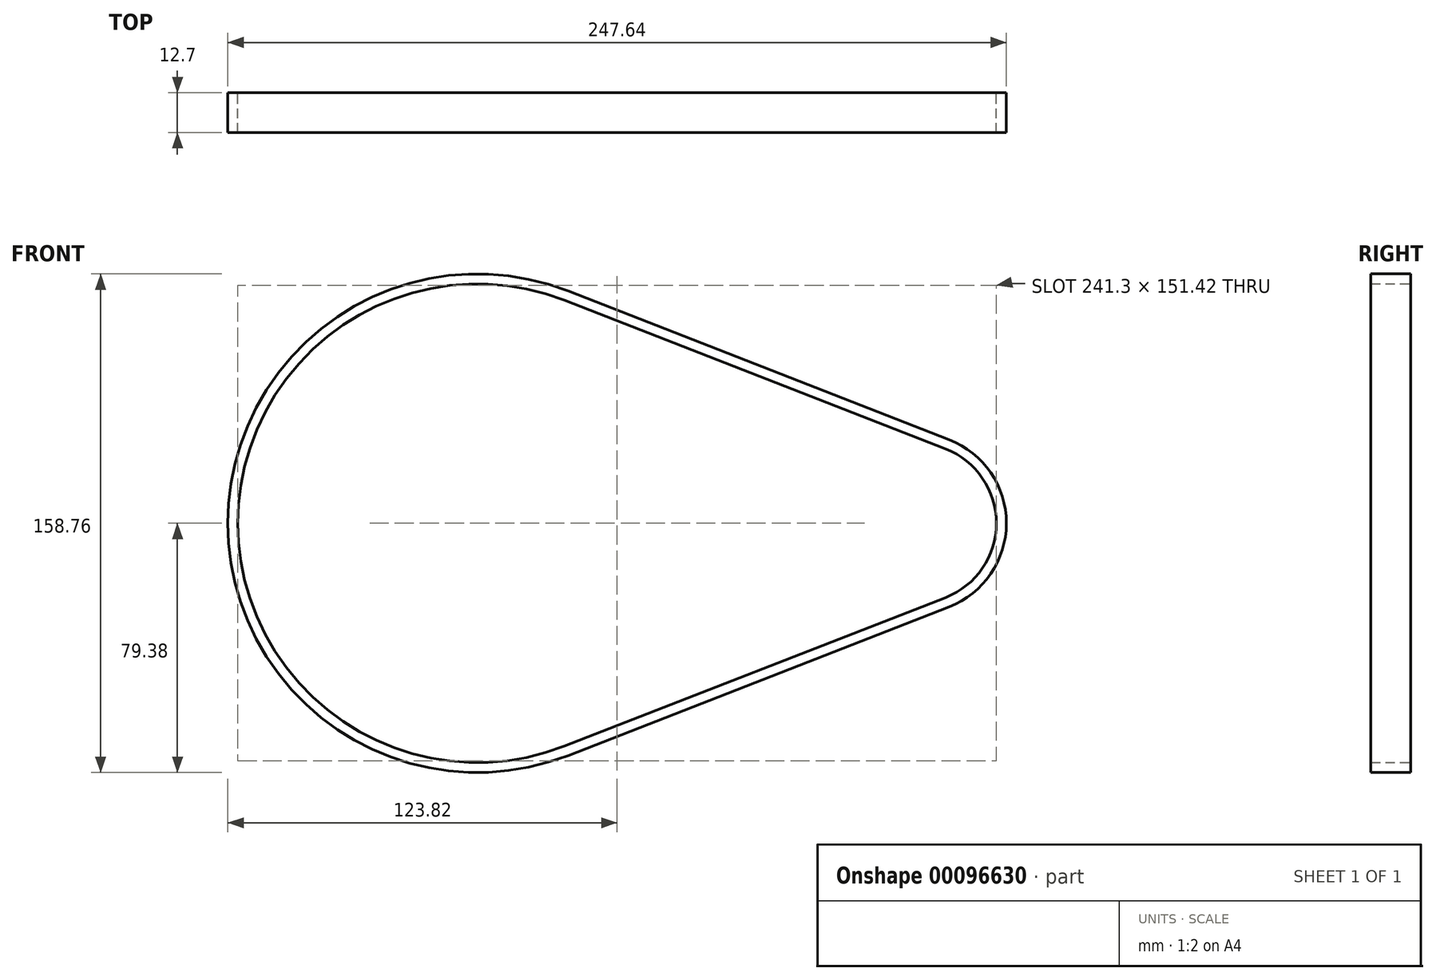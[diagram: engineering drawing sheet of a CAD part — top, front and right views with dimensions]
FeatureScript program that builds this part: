
annotation { "Feature Type Name" : "Feature", "Feature Type Description" : "" }
export const myFeature = defineFeature(function(context is Context, id is Id, definition is map)
    precondition{}
    {
        {
            var Q0;
            Q0=qCreatedBy(makeId("Front.planeOp"),FACE);
            var sketch = newSketch(context, id + "F0", { "sketchPlane" : qUnion([Q0])});
            skArc(sketch, "E0", {"start": v(27.7, 70.98) * mm, "mid": v(-76.2, 0) * mm, "end": v(27.7, -70.98) * mm});
            skArc(sketch, "E1", {"start": v(148.94, -23.66) * mm, "mid": v(165.1, 0) * mm, "end": v(148.94, 23.66) * mm});
            skLineSegment(sketch, "E2", {"start": v(27.7, 70.98) * mm, "end": v(148.94, 23.66) * mm});
            skLineSegment(sketch, "E3", {"start": v(27.7, -70.98) * mm, "end": v(148.94, -23.66) * mm});
            skLineSegment(sketch, "E4.0", {"start": v(28.86, 73.94) * mm, "end": v(150.1, 26.62) * mm});
            skArc(sketch, "E4.1", {"start": v(28.86, 73.94) * mm, "mid": v(-79.37, 0) * mm, "end": v(28.86, -73.94) * mm});
            skLineSegment(sketch, "E4.2", {"start": v(28.86, -73.94) * mm, "end": v(150.1, -26.62) * mm});
            skArc(sketch, "E4.3", {"start": v(150.1, -26.62) * mm, "mid": v(168.28, 0) * mm, "end": v(150.1, 26.62) * mm});
            skSolve(sketch);
        }
        {
            var Q0;
            Q0=makeQuery(id+"F0.imprint","IMPRINT",FACE,{"disambiguationData":[TD([[makeQuery(id+"F0.imprint","IMPRINT",EDGE,{"derivedFrom":sQuery(id+"F0.wireOp",EDGE,"E0")}),-1.0]])]});
            extrude(context, id + "F1", {"entities" : qUnion([Q0]), "depth" : 12.7 * mm});
        }
    });
